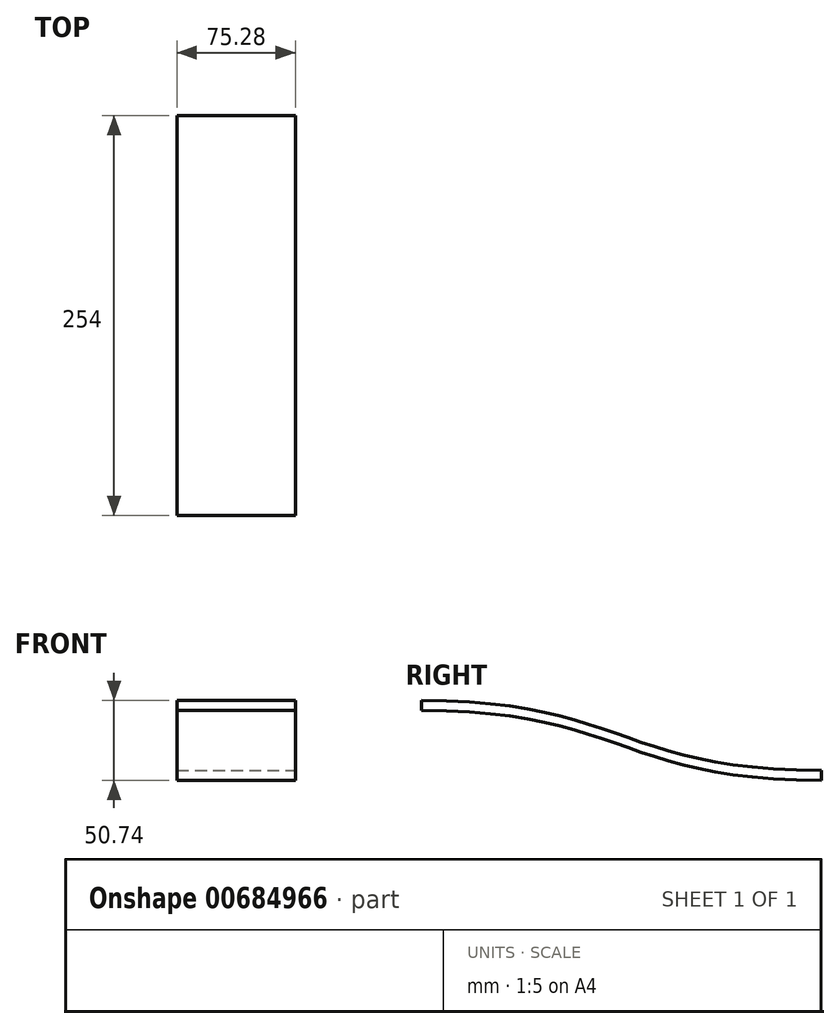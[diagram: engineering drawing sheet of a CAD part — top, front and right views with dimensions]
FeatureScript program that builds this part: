
annotation { "Feature Type Name" : "Feature", "Feature Type Description" : "" }
export const myFeature = defineFeature(function(context is Context, id is Id, definition is map)
    precondition{}
    {
        {
            var Q0;
            Q0=qCreatedBy(makeId("Front.planeOp"),FACE);
            var sketch = newSketch(context, id + "F0", { "sketchPlane" : qUnion([Q0])});
            skLineSegment(sketch, "E0.bottom", {"start": v(-37.64, 47.56) * mm, "end": v(37.64, 47.56) * mm});
            skLineSegment(sketch, "E0.top", {"start": v(-37.64, 41.21) * mm, "end": v(37.64, 41.21) * mm});
            skLineSegment(sketch, "E0.left", {"start": v(-37.64, 47.56) * mm, "end": v(-37.64, 41.21) * mm});
            skLineSegment(sketch, "E0.right", {"start": v(37.64, 47.56) * mm, "end": v(37.64, 41.21) * mm});
            skPoint(sketch, "E0.middle", {"position": v(0, 44.39) * mm});
            skSolve(sketch);
        }
        {
            var Q0;
            Q0=qCreatedBy(makeId("Front.planeOp"),FACE);
            cPlane(context, id + "F1", {"entities" : qUnion([Q0]), "cplaneType" : CPlaneType.OFFSET, "offset" : 254 * mm, "oppositeDirection" : true, "width" : 152.4 * mm, "height" : 152.4 * mm});
        }
        {
            var Q0;
            Q0=qCreatedBy(id+"F1.planeOp",FACE);
            var sketch = newSketch(context, id + "F2", { "sketchPlane" : qUnion([Q0])});
            skLineSegment(sketch, "E1.bottom", {"start": v(-37.64, 3.18) * mm, "end": v(37.64, 3.18) * mm});
            skLineSegment(sketch, "E1.top", {"start": v(-37.64, -3.17) * mm, "end": v(37.64, -3.17) * mm});
            skLineSegment(sketch, "E1.left", {"start": v(-37.64, 3.18) * mm, "end": v(-37.64, -3.17) * mm});
            skLineSegment(sketch, "E1.right", {"start": v(37.64, 3.18) * mm, "end": v(37.64, -3.17) * mm});
            skPoint(sketch, "E1.middle", {"position": v(0, 0) * mm});
            skSolve(sketch);
        }
        {
            var Q0;
            Q0=makeQuery(id+"F2.imprint","IMPRINT",FACE,{"disambiguationData":[TD([[makeQuery(id+"F2.imprint","IMPRINT",EDGE,{"derivedFrom":sQuery(id+"F2.wireOp",EDGE,"E1.bottom")}),-1.0]])]});
            var Q1;
            Q1=makeQuery(id+"F0.imprint","IMPRINT",FACE,{"disambiguationData":[TD([[makeQuery(id+"F0.imprint","IMPRINT",EDGE,{"derivedFrom":sQuery(id+"F0.wireOp",EDGE,"E0.bottom")}),-1.0]])]});
            loft(context, id + "F3", {"startCondition" : LoftEndDerivativeType.NORMAL_TO_PROFILE, "startMagnitude" : 1.5, "endCondition" : LoftEndDerivativeType.NORMAL_TO_PROFILE, "endMagnitude" : 1.5, "sheetProfilesArray" : [{ "sheetProfileEntities" : qUnion([Q0]) }, { "sheetProfileEntities" : qUnion([Q1]) }]});
        }
    });
